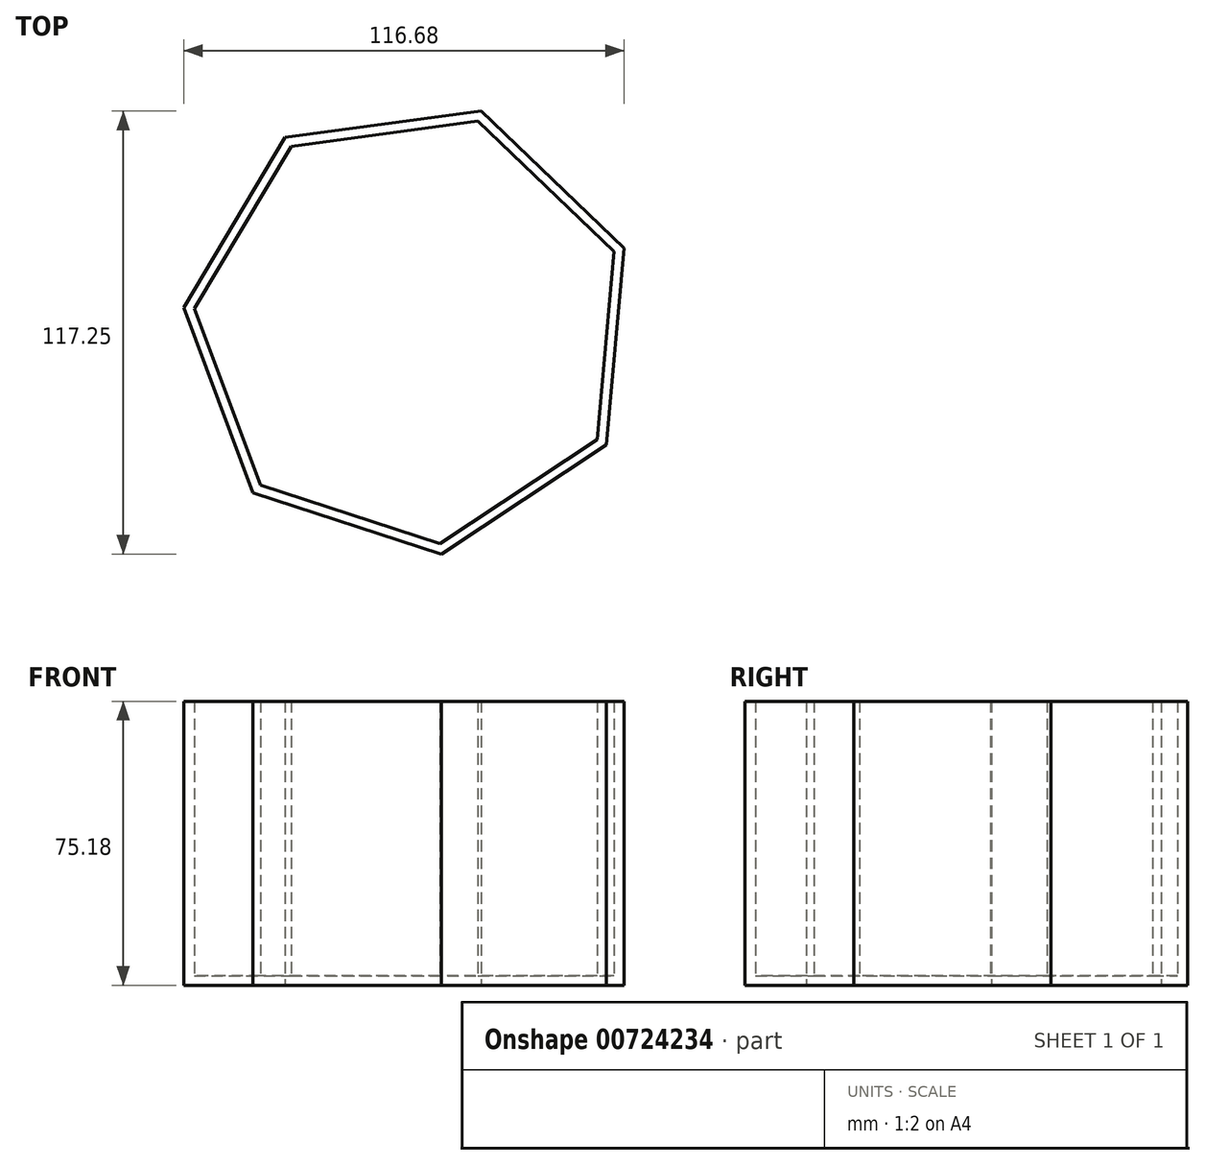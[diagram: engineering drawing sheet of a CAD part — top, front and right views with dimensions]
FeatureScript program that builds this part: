
annotation { "Feature Type Name" : "Feature", "Feature Type Description" : "" }
export const myFeature = defineFeature(function(context is Context, id is Id, definition is map)
    precondition{}
    {
        {
            var Q0;
            Q0=qCreatedBy(makeId("Top.planeOp"),FACE);
            var sketch = newSketch(context, id + "F0", { "sketchPlane" : qUnion([Q0])});
            skCircle(sketch, "E0.cCircle", {"center": v(-5.28, 9.53) * mm, "radius": 54.4 * mm, "construction": true});
            skLineSegment(sketch, "E0.0", {"start": v(-38.52, 59.94) * mm, "end": v(13.4, 66.94) * mm});
            skLineSegment(sketch, "E0.1", {"start": v(13.4, 66.94) * mm, "end": v(51.26, 30.71) * mm});
            skLineSegment(sketch, "E0.2", {"start": v(51.26, 30.71) * mm, "end": v(46.53, -21.47) * mm});
            skLineSegment(sketch, "E0.3", {"start": v(46.53, -21.47) * mm, "end": v(2.8, -50.31) * mm});
            skLineSegment(sketch, "E0.4", {"start": v(2.8, -50.31) * mm, "end": v(-47.03, -34.1) * mm});
            skLineSegment(sketch, "E0.5", {"start": v(-47.03, -34.1) * mm, "end": v(-65.42, 14.97) * mm});
            skLineSegment(sketch, "E0.6", {"start": v(-65.42, 14.97) * mm, "end": v(-38.52, 59.94) * mm});
            skPoint(sketch, "E0.0.midPoint", {"position": v(-12.56, 63.44) * mm});
            skSolve(sketch);
        }
        {
            var Q0;
            Q0=makeQuery(id+"F0.imprint","IMPRINT",FACE,{"disambiguationData":[TD([[makeQuery(id+"F0.imprint","IMPRINT",EDGE,{"derivedFrom":sQuery(id+"F0.wireOp",EDGE,"E0.0")}),-1.0]])]});
            extrude(context, id + "F1", {"entities" : qUnion([Q0]), "depth" : 75.18 * mm, "offsetDistance" : 25.4 * mm});
        }
        {
            var Q0;
            Q0=makeQuery(id+"F1.opExtrude","CAP_FACE",FACE,{"disambiguationData":[OSD([sQuery(id+"F0.wireOp",EDGE,"E0.0"),sQuery(id+"F0.wireOp",EDGE,"E0.1"),sQuery(id+"F0.wireOp",EDGE,"E0.2"),sQuery(id+"F0.wireOp",EDGE,"E0.3"),sQuery(id+"F0.wireOp",EDGE,"E0.4"),sQuery(id+"F0.wireOp",EDGE,"E0.5"),sQuery(id+"F0.wireOp",EDGE,"E0.6")])],"isStart":false});
            shell(context, id + "F2", {"entities" : qUnion([Q0]), "thickness" : 101.6 * mm});
        }
        {
            var Q0;
            Q0=makeQuery(id+"F1.opExtrude","CAP_FACE",FACE,{"disambiguationData":[OSD([sQuery(id+"F0.wireOp",EDGE,"E0.0"),sQuery(id+"F0.wireOp",EDGE,"E0.1"),sQuery(id+"F0.wireOp",EDGE,"E0.2"),sQuery(id+"F0.wireOp",EDGE,"E0.3"),sQuery(id+"F0.wireOp",EDGE,"E0.4"),sQuery(id+"F0.wireOp",EDGE,"E0.5"),sQuery(id+"F0.wireOp",EDGE,"E0.6")])],"isStart":false});
            shell(context, id + "F3", {"entities" : qUnion([Q0]), "thickness" : 2.54 * mm});
        }
    });
